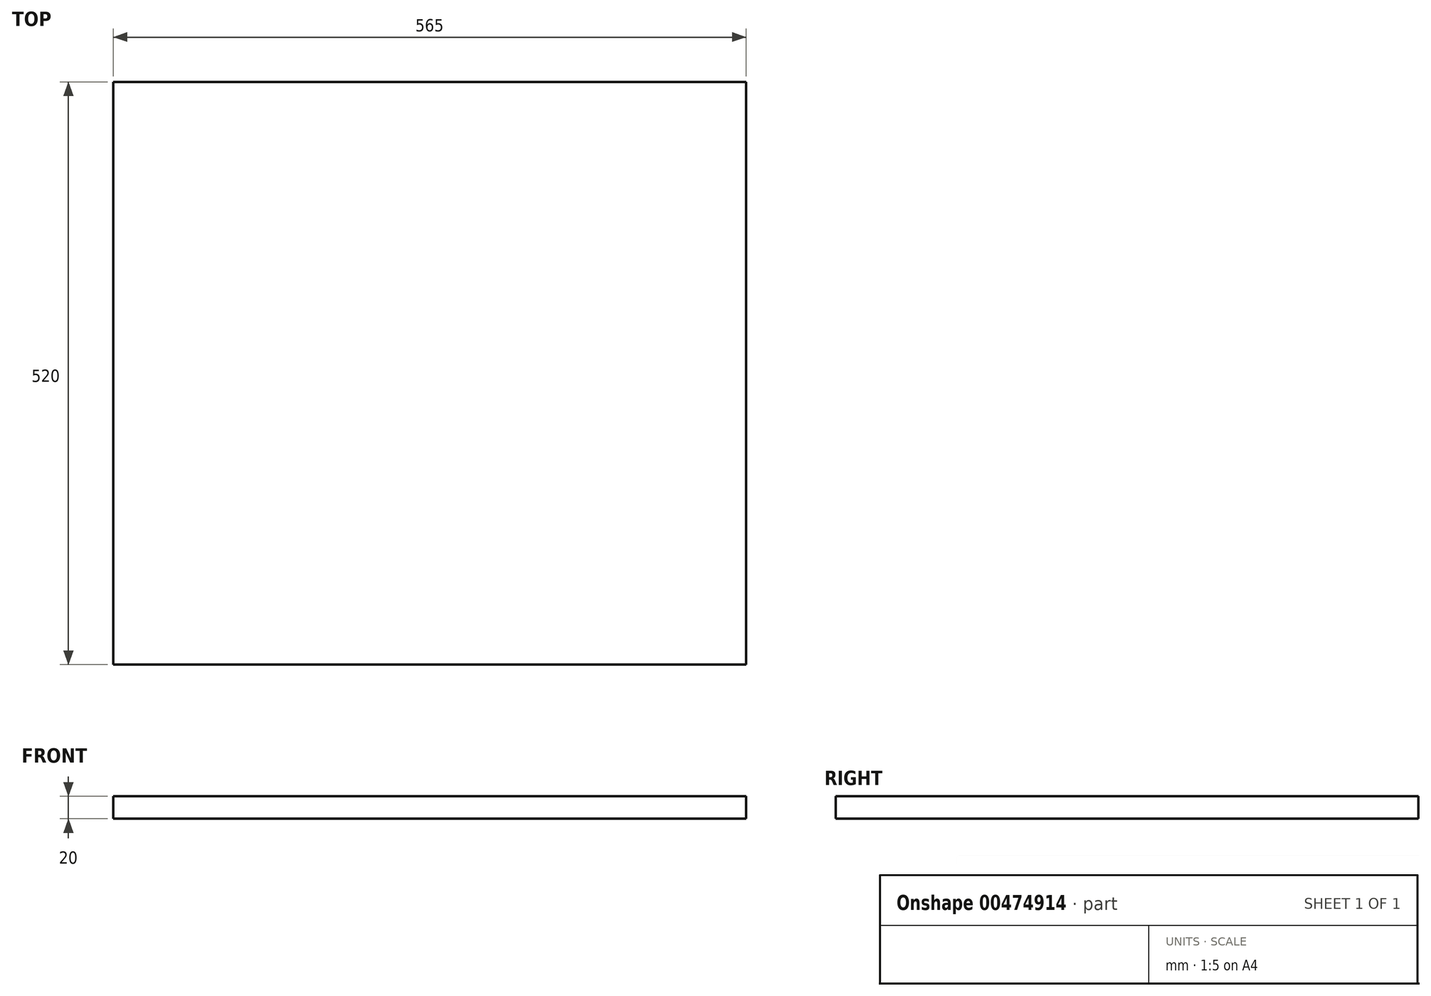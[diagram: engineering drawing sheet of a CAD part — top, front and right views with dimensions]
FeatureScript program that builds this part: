
annotation { "Feature Type Name" : "Feature", "Feature Type Description" : "" }
export const myFeature = defineFeature(function(context is Context, id is Id, definition is map)
    precondition{}
    {
        {
            var Q0;
            Q0=qCreatedBy(makeId("Top.planeOp"),FACE);
            var sketch = newSketch(context, id + "F0", { "sketchPlane" : qUnion([Q0])});
            skLineSegment(sketch, "E0.bottom", {"start": v(-336.36, 196.6) * mm, "end": v(228.64, 196.6) * mm});
            skLineSegment(sketch, "E0.top", {"start": v(-336.36, -323.4) * mm, "end": v(228.64, -323.4) * mm});
            skLineSegment(sketch, "E0.left", {"start": v(-336.36, 196.6) * mm, "end": v(-336.36, -323.4) * mm});
            skLineSegment(sketch, "E0.right", {"start": v(228.64, 196.6) * mm, "end": v(228.64, -323.4) * mm});
            skSolve(sketch);
        }
        {
            var Q0;
            Q0=makeQuery(id+"F0.imprint","IMPRINT",FACE,{"disambiguationData":[TD([[makeQuery(id+"F0.imprint","IMPRINT",EDGE,{"derivedFrom":sQuery(id+"F0.wireOp",EDGE,"E0.bottom")}),-1.0]])]});
            extrude(context, id + "F1", {"entities" : qUnion([Q0]), "depth" : 20 * mm, "offsetDistance" : 25 * mm});
        }
    });
